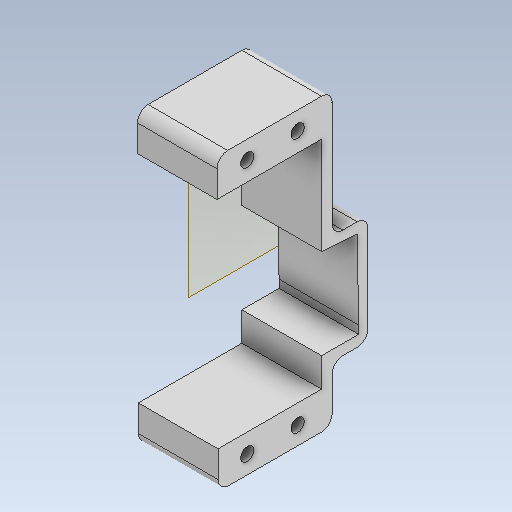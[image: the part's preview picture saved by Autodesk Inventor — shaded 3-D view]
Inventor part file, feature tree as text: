
AUTODESK INVENTOR PART (.ipt)
format: ipt  version: 2020 (Build 240168000, 168)  size: 158,720 bytes
history: native  units: mm
features: reference x5, other x4, sketch x2, plane x1, extrude x1, hole x1, fillet x1
ambient origin geometry x8: Origin, YZ Plane, XZ Plane, XY Plane, X Axis, Y Axis, Z Axis, Center Point
bodies: Solid1 (feature_tree)
feature tree (15):
  plane  "Work Plane1"
  extrude  "Extrusion1"  Depth=19.5mm
  hole  "Hole1"  [1 undecoded]
  fillet  "Fillet1"  Radius=2.0mm
  sketch  "Sketch1"  dims[d0=-15.5mm d1=19.5mm]
  reference  "Reference1"
  reference  "Reference2"
  reference  "Reference3"
  reference  "Reference4"
  reference  "Reference5"
  sketch  "Sketch2"  dims[d2=2.0mm d3=2.0mm d4=2.0mm d5=7.0mm d6=7.0mm d7=2.0mm d8=8.0mm d9=40.8mm d10=15.0mm d11=0.0mm d12=4.5mm d13=9.5mm d14=4.5mm d15=9.5mm d16=48.0mm d17=3.4mm d18=3.4mm d19=2.5mm d20=6.0mm d21=5.0mm d22=2.0mm d23=90.0deg d24=8.0mm d25=20.594885mm d26=2.0mm]
  parser-record x1  (decoder bookkeeping rows leaked as tree rows — omitted from the tree; the rows remain in map.json)
  other  "motorized.iam"
  other  "funnel:1"
  other  "fence:1"
note: 1 required parameter value undecoded (feature->parameter linkage not recoverable at this tier; creation-order binding heuristic only, values carry confidence <= 0.55)
note: 1 file-system path scrubbed to <path> (originals preserved in map.json)
